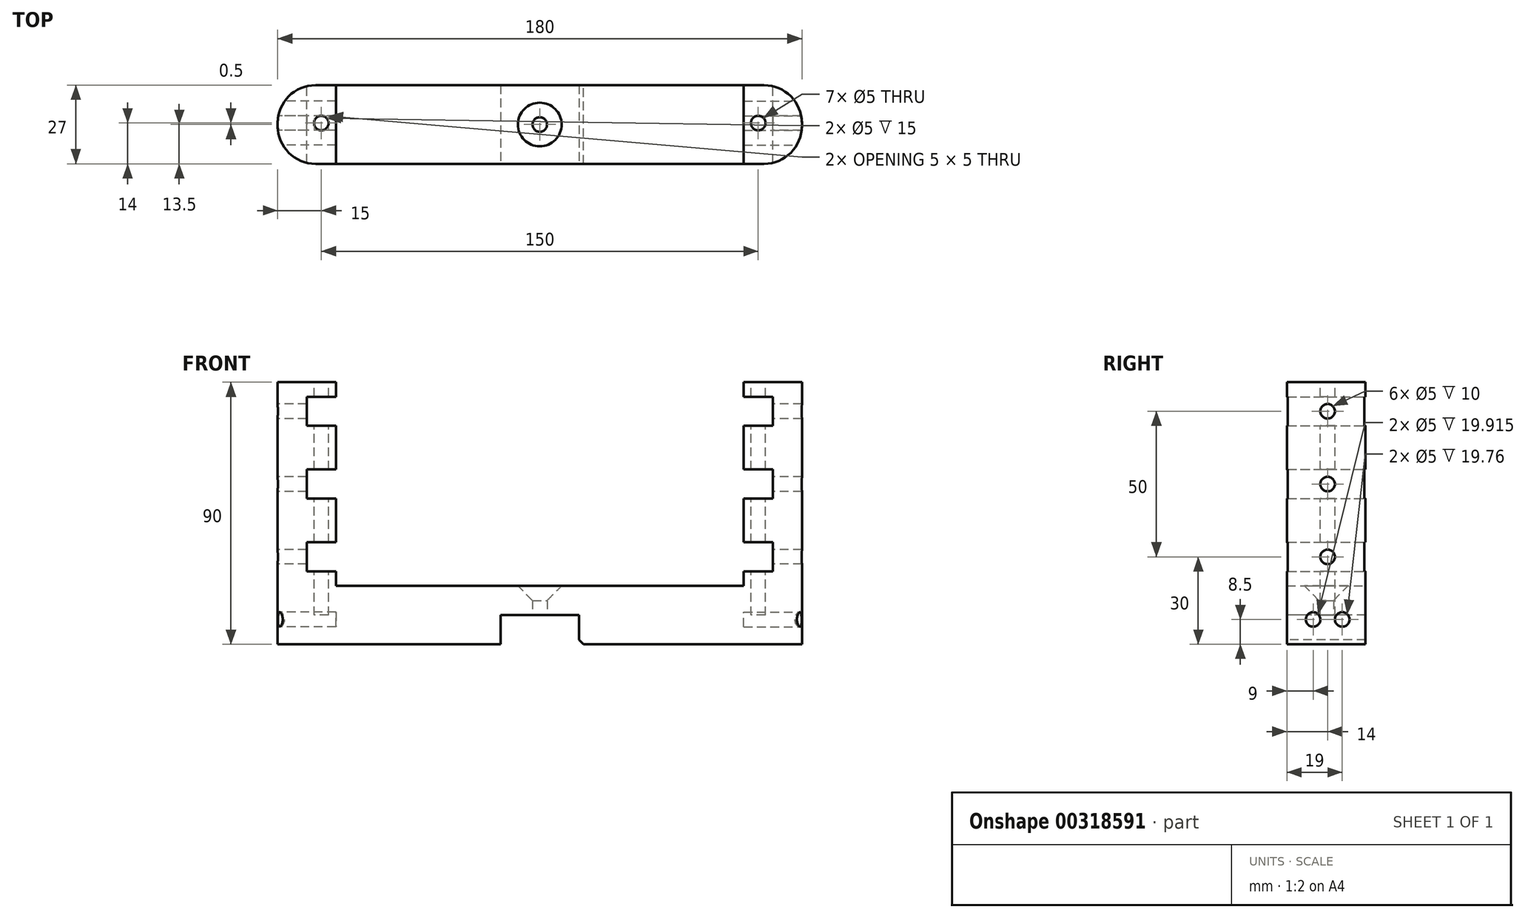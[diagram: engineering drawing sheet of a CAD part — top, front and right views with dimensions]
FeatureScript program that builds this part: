
annotation { "Feature Type Name" : "Feature", "Feature Type Description" : "" }
export const myFeature = defineFeature(function(context is Context, id is Id, definition is map)
    precondition{}
    {
        {
            var Q0;
            Q0=qCreatedBy(makeId("Front.planeOp"),FACE);
            var sketch = newSketch(context, id + "F0", { "sketchPlane" : qUnion([Q0])});
            skLineSegment(sketch, "E0.bottom", {"start": v(0, 0) * mm, "end": v(180, 0) * mm});
            skLineSegment(sketch, "E0.top", {"start": v(0, 90) * mm, "end": v(180, 90) * mm});
            skLineSegment(sketch, "E0.left", {"start": v(0, 0) * mm, "end": v(0, 90) * mm});
            skLineSegment(sketch, "E0.right", {"start": v(180, 0) * mm, "end": v(180, 90) * mm});
            skSolve(sketch);
        }
        {
            var Q0;
            Q0=makeQuery(id+"F0.imprint","IMPRINT",FACE,{"disambiguationData":[TD([[makeQuery(id+"F0.imprint","IMPRINT",EDGE,{"derivedFrom":sQuery(id+"F0.wireOp",EDGE,"E0.bottom")}),1.0]])]});
            extrude(context, id + "F1", {"entities" : qUnion([Q0]), "depth" : 27 * mm});
        }
        {
            var Q0;
            Q0=qCreatedBy(makeId("Front.planeOp"),FACE);
            var sketch = newSketch(context, id + "F2", { "sketchPlane" : qUnion([Q0])});
            skLineSegment(sketch, "E1.bottom", {"start": v(20, 90) * mm, "end": v(160, 90) * mm});
            skLineSegment(sketch, "E1.top", {"start": v(20, 20) * mm, "end": v(160, 20) * mm});
            skLineSegment(sketch, "E1.left", {"start": v(20, 90) * mm, "end": v(20, 20) * mm});
            skLineSegment(sketch, "E1.right", {"start": v(160, 90) * mm, "end": v(160, 20) * mm});
            skSolve(sketch);
        }
        {
            var Q0;
            Q0=makeQuery(id+"F2.imprint","IMPRINT",FACE,{"disambiguationData":[TD([[makeQuery(id+"F2.imprint","IMPRINT",EDGE,{"derivedFrom":sQuery(id+"F2.wireOp",EDGE,"E1.bottom")}),-1.0]])]});
            extrude(context, id + "F3", {"entities" : qUnion([Q0]), "operationType" : NewBodyOperationType.REMOVE, "endBound" : BoundingType.THROUGH_ALL, "depth" : 25 * mm});
        }
        {
            var Q0;
            Q0=qCreatedBy(makeId("Front.planeOp"),FACE);
            var sketch = newSketch(context, id + "F4", { "sketchPlane" : qUnion([Q0])});
            skLineSegment(sketch, "E2.bottom", {"start": v(170, 85) * mm, "end": v(160, 85) * mm});
            skLineSegment(sketch, "E2.top", {"start": v(170, 75) * mm, "end": v(160, 75) * mm});
            skLineSegment(sketch, "E2.left", {"start": v(170, 85) * mm, "end": v(170, 75) * mm});
            skLineSegment(sketch, "E2.right", {"start": v(160, 85) * mm, "end": v(160, 75) * mm});
            skLineSegment(sketch, "E3.bottom", {"start": v(170, 60) * mm, "end": v(160, 60) * mm});
            skLineSegment(sketch, "E3.top", {"start": v(170, 50) * mm, "end": v(160, 50) * mm});
            skLineSegment(sketch, "E3.left", {"start": v(170, 60) * mm, "end": v(170, 50) * mm});
            skLineSegment(sketch, "E3.right", {"start": v(160, 60) * mm, "end": v(160, 50) * mm});
            skLineSegment(sketch, "E4.bottom", {"start": v(170, 35) * mm, "end": v(160, 35) * mm});
            skLineSegment(sketch, "E4.top", {"start": v(170, 25) * mm, "end": v(160, 25) * mm});
            skLineSegment(sketch, "E4.left", {"start": v(170, 35) * mm, "end": v(170, 25) * mm});
            skLineSegment(sketch, "E4.right", {"start": v(160, 35) * mm, "end": v(160, 25) * mm});
            skLineSegment(sketch, "E5.bottom", {"start": v(20, 85) * mm, "end": v(10, 85) * mm});
            skLineSegment(sketch, "E5.top", {"start": v(20, 75) * mm, "end": v(10, 75) * mm});
            skLineSegment(sketch, "E5.left", {"start": v(20, 85) * mm, "end": v(20, 75) * mm});
            skLineSegment(sketch, "E5.right", {"start": v(10, 85) * mm, "end": v(10, 75) * mm});
            skLineSegment(sketch, "E6.bottom", {"start": v(20, 60) * mm, "end": v(10, 60) * mm});
            skLineSegment(sketch, "E6.top", {"start": v(20, 50) * mm, "end": v(10, 50) * mm});
            skLineSegment(sketch, "E6.left", {"start": v(20, 60) * mm, "end": v(20, 50) * mm});
            skLineSegment(sketch, "E6.right", {"start": v(10, 60) * mm, "end": v(10, 50) * mm});
            skLineSegment(sketch, "E7.bottom", {"start": v(20, 35) * mm, "end": v(10, 35) * mm});
            skLineSegment(sketch, "E7.top", {"start": v(20, 25) * mm, "end": v(10, 25) * mm});
            skLineSegment(sketch, "E7.left", {"start": v(20, 35) * mm, "end": v(20, 25) * mm});
            skLineSegment(sketch, "E7.right", {"start": v(10, 35) * mm, "end": v(10, 25) * mm});
            skLineSegment(sketch, "E8", {"start": v(170, 90) * mm, "end": v(170, 40) * mm, "construction": true});
            skLineSegment(sketch, "E9", {"start": v(10, 90) * mm, "end": v(10, 85) * mm, "construction": true});
            skSolve(sketch);
        }
        {
            var Q0;
            Q0=makeQuery(id+"F4.imprint","IMPRINT",FACE,{"disambiguationData":[TD([[makeQuery(id+"F4.imprint","IMPRINT",EDGE,{"derivedFrom":sQuery(id+"F4.wireOp",EDGE,"E2.bottom")}),1.0]])]});
            var Q1;
            Q1=makeQuery(id+"F4.imprint","IMPRINT",FACE,{"disambiguationData":[TD([[makeQuery(id+"F4.imprint","IMPRINT",EDGE,{"derivedFrom":sQuery(id+"F4.wireOp",EDGE,"E3.bottom")}),1.0]])]});
            var Q2;
            Q2=makeQuery(id+"F4.imprint","IMPRINT",FACE,{"disambiguationData":[TD([[makeQuery(id+"F4.imprint","IMPRINT",EDGE,{"derivedFrom":sQuery(id+"F4.wireOp",EDGE,"E4.bottom")}),1.0]])]});
            var Q3;
            Q3=makeQuery(id+"F4.imprint","IMPRINT",FACE,{"disambiguationData":[TD([[makeQuery(id+"F4.imprint","IMPRINT",EDGE,{"derivedFrom":sQuery(id+"F4.wireOp",EDGE,"E7.bottom")}),1.0]])]});
            var Q4;
            Q4=makeQuery(id+"F4.imprint","IMPRINT",FACE,{"disambiguationData":[TD([[makeQuery(id+"F4.imprint","IMPRINT",EDGE,{"derivedFrom":sQuery(id+"F4.wireOp",EDGE,"E6.bottom")}),1.0]])]});
            var Q5;
            Q5=makeQuery(id+"F4.imprint","IMPRINT",FACE,{"disambiguationData":[TD([[makeQuery(id+"F4.imprint","IMPRINT",EDGE,{"derivedFrom":sQuery(id+"F4.wireOp",EDGE,"E5.bottom")}),1.0]])]});
            extrude(context, id + "F5", {"entities" : qUnion([Q0, Q1, Q2, Q3, Q4, Q5]), "operationType" : NewBodyOperationType.REMOVE, "endBound" : BoundingType.THROUGH_ALL, "depth" : 25 * mm});
        }
        {
            var Q0;
            {var subQ0=sQuery(id+"F0.wireOp",EDGE,"E0.right");var subQ2=sQuery(id+"F0.wireOp",EDGE,"E0.top");Q0=makeQuery(id+"F3.boolean.opBoolean","SPLIT",FACE,{"disambiguationData":[TD([makeQuery(id+"F1.opExtrude","SWEPT_FACE",FACE,{"disambiguationData":[OSD([subQ0])]})])],"derivedFrom":makeQuery(id+"F1.opExtrude","SWEPT_FACE",FACE,{"disambiguationData":[OSD([subQ2])]})});}
            var sketch = newSketch(context, id + "F6", { "sketchPlane" : qUnion([Q0])});
            skCircle(sketch, "E10", {"center": v(165, -13) * mm, "radius": 2.5 * mm});
            skCircle(sketch, "E11", {"center": v(15, -13) * mm, "radius": 2.5 * mm});
            skLineSegment(sketch, "E12", {"start": v(90, 0) * mm, "end": v(90, -27) * mm, "construction": true});
            skSolve(sketch);
        }
        {
            var Q0;
            Q0=makeQuery(id+"F6.imprint","IMPRINT",FACE,{"disambiguationData":[TD([[makeQuery(id+"F6.imprint","IMPRINT",EDGE,{"derivedFrom":sQuery(id+"F6.wireOp",EDGE,"E10")}),1.0]])]});
            var Q1;
            Q1=makeQuery(id+"F6.imprint","IMPRINT",FACE,{"disambiguationData":[TD([[makeQuery(id+"F6.imprint","IMPRINT",EDGE,{"derivedFrom":sQuery(id+"F6.wireOp",EDGE,"E11")}),1.0]])]});
            extrude(context, id + "F7", {"entities" : qUnion([Q0, Q1]), "operationType" : NewBodyOperationType.REMOVE, "oppositeDirection" : true, "depth" : 80 * mm});
        }
        {
            var Q0;
            Q0=qCreatedBy(makeId("Right.planeOp"),FACE);
            var sketch = newSketch(context, id + "F8", { "sketchPlane" : qUnion([Q0])});
            skCircle(sketch, "E13", {"center": v(-13, 80) * mm, "radius": 2.5 * mm});
            skCircle(sketch, "E14", {"center": v(-13, 55) * mm, "radius": 2.5 * mm});
            skCircle(sketch, "E15", {"center": v(-13, 30) * mm, "radius": 2.5 * mm});
            skLineSegment(sketch, "E16", {"start": v(-27, 30) * mm, "end": v(0, 30) * mm, "construction": true});
            skLineSegment(sketch, "E17", {"start": v(-27, 55) * mm, "end": v(0, 55) * mm, "construction": true});
            skLineSegment(sketch, "E18", {"start": v(-13, 0) * mm, "end": v(-13, 90) * mm});
            skSolve(sketch);
        }
        {
            var Q0;
            Q0=makeQuery(id+"F8.imprint","IMPRINT",FACE,{"disambiguationData":[TD([[makeQuery(id+"F8.imprint","IMPRINT",EDGE,{"derivedFrom":sQuery(id+"F8.wireOp",EDGE,"E13")}),1.0]])]});
            var Q1;
            Q1=makeQuery(id+"F8.imprint","IMPRINT",FACE,{"disambiguationData":[TD([[makeQuery(id+"F8.imprint","IMPRINT",EDGE,{"derivedFrom":sQuery(id+"F8.wireOp",EDGE,"E14")}),1.0]])]});
            var Q2;
            Q2=makeQuery(id+"F8.imprint","IMPRINT",FACE,{"disambiguationData":[TD([[makeQuery(id+"F8.imprint","IMPRINT",EDGE,{"derivedFrom":sQuery(id+"F8.wireOp",EDGE,"E15")}),1.0]])]});
            extrude(context, id + "F9", {"entities" : qUnion([Q0, Q1, Q2]), "operationType" : NewBodyOperationType.REMOVE, "endBound" : BoundingType.THROUGH_ALL, "depth" : 25 * mm});
        }
        {
            var Q0;
            Q0=qCreatedBy(makeId("Right.planeOp"),FACE);
            var sketch = newSketch(context, id + "F10", { "sketchPlane" : qUnion([Q0])});
            skCircle(sketch, "E19", {"center": v(-8, 8.5) * mm, "radius": 2.5 * mm});
            skCircle(sketch, "E20", {"center": v(-18, 8.5) * mm, "radius": 2.5 * mm});
            skSolve(sketch);
        }
        {
            var Q0;
            Q0=makeQuery(id+"F10.imprint","IMPRINT",FACE,{"disambiguationData":[TD([[makeQuery(id+"F10.imprint","IMPRINT",EDGE,{"derivedFrom":sQuery(id+"F10.wireOp",EDGE,"E19")}),1.0]])]});
            var Q1;
            Q1=makeQuery(id+"F10.imprint","IMPRINT",FACE,{"disambiguationData":[TD([[makeQuery(id+"F10.imprint","IMPRINT",EDGE,{"derivedFrom":sQuery(id+"F10.wireOp",EDGE,"E20")}),1.0]])]});
            extrude(context, id + "F11", {"entities" : qUnion([Q0, Q1]), "operationType" : NewBodyOperationType.REMOVE, "depth" : 20 * mm});
        }
        {
            var Q0;
            Q0=makeQuery(id+"F1.opExtrude","SWEPT_FACE",FACE,{"disambiguationData":[OSD([sQuery(id+"F0.wireOp",EDGE,"E0.right")])]});
            var sketch = newSketch(context, id + "F12", { "sketchPlane" : qUnion([Q0])});
            skCircle(sketch, "E21", {"center": v(-18, 8.5) * mm, "radius": 2.5 * mm});
            skCircle(sketch, "E22", {"center": v(-8, 8.5) * mm, "radius": 2.5 * mm});
            skSolve(sketch);
        }
        {
            var Q0;
            Q0=makeQuery(id+"F12.imprint","IMPRINT",FACE,{"disambiguationData":[TD([[makeQuery(id+"F12.imprint","IMPRINT",EDGE,{"derivedFrom":sQuery(id+"F12.wireOp",EDGE,"E22")}),1.0]])]});
            var Q1;
            Q1=makeQuery(id+"F12.imprint","IMPRINT",FACE,{"disambiguationData":[TD([[makeQuery(id+"F12.imprint","IMPRINT",EDGE,{"derivedFrom":sQuery(id+"F12.wireOp",EDGE,"E21")}),1.0]])]});
            extrude(context, id + "F13", {"entities" : qUnion([Q0, Q1]), "operationType" : NewBodyOperationType.REMOVE, "oppositeDirection" : true, "depth" : 20 * mm});
        }
        {
            var Q0;
            Q0=makeQuery(id+"F1.opExtrude","CAP_EDGE",EDGE,{"disambiguationData":[OSD([sQuery(id+"F0.wireOp",EDGE,"E0.left")])],"isStart":true});
            var Q1;
            Q1=makeQuery(id+"F1.opExtrude","CAP_EDGE",EDGE,{"disambiguationData":[OSD([sQuery(id+"F0.wireOp",EDGE,"E0.left")])],"isStart":false});
            var Q2;
            Q2=makeQuery(id+"F1.opExtrude","CAP_EDGE",EDGE,{"disambiguationData":[OSD([sQuery(id+"F0.wireOp",EDGE,"E0.right")])],"isStart":false});
            var Q3;
            Q3=makeQuery(id+"F1.opExtrude","CAP_EDGE",EDGE,{"disambiguationData":[OSD([sQuery(id+"F0.wireOp",EDGE,"E0.right")])],"isStart":true});
            fillet(context, id + "F14", {"entities" : qUnion([Q0, Q1, Q2, Q3]), "radius" : 13 * mm, "tangentPropagation" : true, "allowEdgeOverflow" : false});
        }
        {
            var Q0;
            Q0=makeQuery(id+"F14.opFillet","SPLIT",FACE,{"disambiguationData":[OD(6.0)],"derivedFrom":makeQuery(id+"F1.opExtrude","CAP_FACE",FACE,{"disambiguationData":[OSD([sQuery(id+"F0.wireOp",EDGE,"E0.bottom"),sQuery(id+"F0.wireOp",EDGE,"E0.top"),sQuery(id+"F0.wireOp",EDGE,"E0.left"),sQuery(id+"F0.wireOp",EDGE,"E0.right")])],"isStart":false})});
            var sketch = newSketch(context, id + "F15", { "sketchPlane" : qUnion([Q0])});
            skLineSegment(sketch, "E23", {"start": v(76.5, 0) * mm, "end": v(76.5, 10) * mm});
            skLineSegment(sketch, "E24", {"start": v(76.5, 10) * mm, "end": v(103.5, 10) * mm});
            skLineSegment(sketch, "E25", {"start": v(103.5, 10) * mm, "end": v(103.5, 0) * mm});
            skPoint(sketch, "E25.endSnap0", {"position": v(90, 0) * mm});
            skSolve(sketch);
        }
        {
            var Q0;
            {var subQ0=sQuery(id+"F15.wireOp",EDGE,"E23");Q0=makeQuery(id+"F15.imprint","IMPRINT",FACE,{"disambiguationData":[TD([[makeQuery(id+"F15.imprint","IMPRINT",EDGE,{"derivedFrom":subQ0}),-1.0]])]});}
            extrude(context, id + "F16", {"entities" : qUnion([Q0]), "operationType" : NewBodyOperationType.REMOVE, "endBound" : BoundingType.THROUGH_ALL, "oppositeDirection" : true, "depth" : 25 * mm});
        }
        {
            var Q0;
            Q0=qCreatedBy(makeId("Top.planeOp"),FACE);
            var sketch = newSketch(context, id + "F17", { "sketchPlane" : qUnion([Q0])});
            skCircle(sketch, "E26", {"center": v(90, -13.5) * mm, "radius": 2.5 * mm});
            skLineSegment(sketch, "E27", {"start": v(10, -13.5) * mm, "end": v(170, -13.5) * mm});
            skSolve(sketch);
        }
        {
            var Q0;
            {var subQ0=sQuery(id+"F17.wireOp",EDGE,"E27");var subQ1=sQuery(id+"F17.wireOp",EDGE,"E26");var subQ2=makeQuery(id+"F17.imprint","INTERSECT",VERTEX,{"disambiguationData":[OD(0.0)],"derivedFrom":[subQ1,subQ0]});Q0=makeQuery(id+"F17.imprint","IMPRINT",FACE,{"disambiguationData":[TD([[makeQuery(id+"F17.imprint","IMPRINT",EDGE,{"disambiguationData":[TD([[subQ2,-1.0]])],"derivedFrom":subQ1}),1.0]])]});}
            var Q1;
            {var subQ0=sQuery(id+"F17.wireOp",EDGE,"E27");var subQ1=sQuery(id+"F17.wireOp",EDGE,"E26");var subQ2=makeQuery(id+"F17.imprint","INTERSECT",VERTEX,{"disambiguationData":[OD(0.0)],"derivedFrom":[subQ1,subQ0]});Q1=makeQuery(id+"F17.imprint","IMPRINT",FACE,{"disambiguationData":[TD([[makeQuery(id+"F17.imprint","IMPRINT",EDGE,{"disambiguationData":[TD([[subQ2,1.0]])],"derivedFrom":subQ1}),1.0]])]});}
            extrude(context, id + "F18", {"entities" : qUnion([Q0, Q1]), "operationType" : NewBodyOperationType.REMOVE, "endBound" : BoundingType.THROUGH_ALL, "depth" : 25 * mm});
        }
        {
            var Q0;
            Q0=makeQuery(id+"F16.boolean.opBoolean","COPY",EDGE,{"derivedFrom":makeQuery(id+"F16.opExtrude","SWEPT_EDGE",EDGE,{"disambiguationData":[OSD([sQuery(id+"F0.wireOp",EDGE,"E0.bottom"),sQuery(id+"F15.wireOp",EDGE,"E23")])]})});
            var Q1;
            Q1=makeQuery(id+"F16.boolean.opBoolean","COPY",EDGE,{"derivedFrom":makeQuery(id+"F16.opExtrude","SWEPT_EDGE",EDGE,{"disambiguationData":[OSD([sQuery(id+"F0.wireOp",EDGE,"E0.bottom"),sQuery(id+"F15.wireOp",EDGE,"E25")])]})});
            chamfer(context, id + "F19", {"entities" : qUnion([Q0, Q1]), "width" : 1.5 * mm, "tangentPropagation" : true});
        }
        {
            var Q0;
            Q0=makeQuery(id+"F18.boolean.opBoolean","INTERSECT",EDGE,{"derivedFrom":[makeQuery(id+"F3.boolean.opBoolean","COPY",FACE,{"derivedFrom":makeQuery(id+"F3.opExtrude","SWEPT_FACE",FACE,{"disambiguationData":[OSD([sQuery(id+"F2.wireOp",EDGE,"E1.top")])]})}),makeQuery(id+"F18.opExtrude","SWEPT_FACE",FACE,{"disambiguationData":[OSD([sQuery(id+"F17.wireOp",EDGE,"E26")])]})]});
            chamfer(context, id + "F20", {"entities" : qUnion([Q0]), "width" : 5 * mm, "tangentPropagation" : true});
        }
    });
